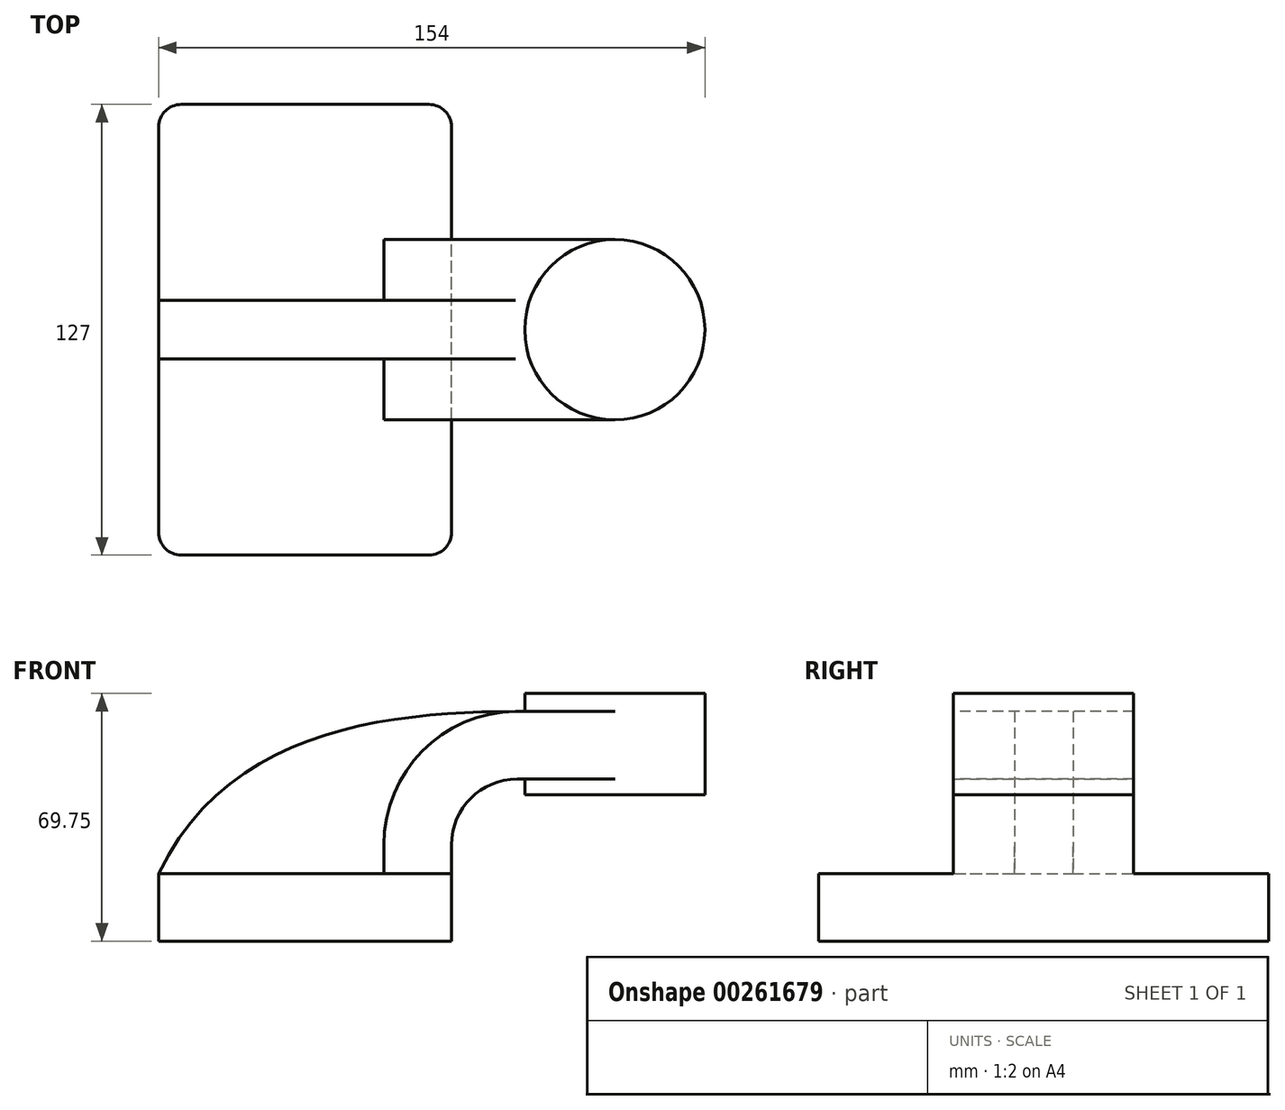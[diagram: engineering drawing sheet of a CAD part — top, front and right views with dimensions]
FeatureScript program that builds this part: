
annotation { "Feature Type Name" : "Feature", "Feature Type Description" : "" }
export const myFeature = defineFeature(function(context is Context, id is Id, definition is map)
    precondition{}
    {
        {
            var Q0;
            Q0=qCreatedBy(makeId("Front.planeOp"),FACE);
            var sketch = newSketch(context, id + "F0", { "sketchPlane" : qUnion([Q0])});
            skLineSegment(sketch, "E0.bottom", {"start": v(-41.28, -9.53) * mm, "end": v(41.28, -9.53) * mm});
            skLineSegment(sketch, "E0.top", {"start": v(-41.28, 9.53) * mm, "end": v(41.28, 9.53) * mm});
            skLineSegment(sketch, "E0.left", {"start": v(-41.28, -9.53) * mm, "end": v(-41.28, 9.53) * mm});
            skLineSegment(sketch, "E0.right", {"start": v(41.28, -9.53) * mm, "end": v(41.28, 9.53) * mm});
            skPoint(sketch, "E0.middle", {"position": v(0, 0) * mm});
            skLineSegment(sketch, "E1.bottom", {"start": v(112.72, 31.64) * mm, "end": v(61.92, 31.64) * mm});
            skLineSegment(sketch, "E1.top", {"start": v(112.72, 60.22) * mm, "end": v(61.92, 60.22) * mm});
            skLineSegment(sketch, "E1.left", {"start": v(112.72, 31.64) * mm, "end": v(112.72, 60.22) * mm});
            skLineSegment(sketch, "E1.right", {"start": v(61.92, 31.64) * mm, "end": v(61.92, 60.22) * mm});
            skPoint(sketch, "E1.middle", {"position": v(87.32, 45.93) * mm});
            skLineSegment(sketch, "E2", {"start": v(41.28, 9.53) * mm, "end": v(41.28, 17.63) * mm});
            skArc(sketch, "E3", {"start": v(41.28, 17.63) * mm, "mid": v(46.7, 30.71) * mm, "end": v(59.78, 36.13) * mm});
            skLineSegment(sketch, "E4", {"start": v(59.78, 36.13) * mm, "end": v(87.32, 36.13) * mm});
            skArc(sketch, "E5.1", {"start": v(22.23, 17.63) * mm, "mid": v(33.22, 44.18) * mm, "end": v(59.78, 55.18) * mm});
            skLineSegment(sketch, "E5.2", {"start": v(22.23, 9.53) * mm, "end": v(22.23, 17.63) * mm});
            skPoint(sketch, "E6.endSnap0", {"position": v(87.32, 31.64) * mm});
            skLineSegment(sketch, "E7", {"start": v(59.78, 55.18) * mm, "end": v(87.32, 55.18) * mm});
            skLineSegment(sketch, "E8", {"start": v(87.32, 60.22) * mm, "end": v(87.32, 31.64) * mm});
            skFitSpline(sketch, "E9", {"points": [v(59.78, 55.18) * mm, v(-41.28, 9.53) * mm], "startDerivative": vector(-106.5, -0.65) * mm, "endDerivative": vector(-59.81, -124.07) * mm});
            skSolve(sketch);
        }
        {
            var Q0;
            Q0=makeQuery(id+"F0.imprint","IMPRINT",FACE,{"disambiguationData":[TD([[makeQuery(id+"F0.imprint","IMPRINT",EDGE,{"derivedFrom":sQuery(id+"F0.wireOp",EDGE,"E0.bottom")}),1.0]])]});
            extrude(context, id + "F1", {"entities" : qUnion([Q0]), "endBound" : BoundingType.SYMMETRIC, "depth" : 127 * mm});
        }
        {
            var Q0;
            {var subQ6=sQuery(id+"F0.wireOp",EDGE,"E2");Q0=makeQuery(id+"F0.imprint","IMPRINT",FACE,{"disambiguationData":[TD([[makeQuery(id+"F0.imprint","IMPRINT",EDGE,{"derivedFrom":subQ6}),1.0]])]});}
            var Q1;
            {var subQ0=sQuery(id+"F0.wireOp",EDGE,"E4");var subQ1=sQuery(id+"F0.wireOp",EDGE,"E1.right");var subQ2=makeQuery(id+"F0.imprint","INTERSECT",VERTEX,{"derivedFrom":[subQ1,subQ0]});Q1=makeQuery(id+"F0.imprint","IMPRINT",FACE,{"disambiguationData":[TD([[makeQuery(id+"F0.imprint","IMPRINT",EDGE,{"disambiguationData":[TD([[subQ2,-1.0]])],"derivedFrom":subQ1}),-1.0]])]});}
            extrude(context, id + "F2", {"entities" : qUnion([Q0, Q1]), "operationType" : NewBodyOperationType.ADD, "endBound" : BoundingType.SYMMETRIC, "depth" : 50.8 * mm});
        }
        {
            var Q0;
            {var subQ3=sQuery(id+"F0.wireOp",EDGE,"E5.2");Q0=makeQuery(id+"F0.imprint","IMPRINT",FACE,{"disambiguationData":[TD([[makeQuery(id+"F0.imprint","IMPRINT",EDGE,{"derivedFrom":subQ3}),1.0]])]});}
            extrude(context, id + "F3", {"entities" : qUnion([Q0]), "operationType" : NewBodyOperationType.ADD, "endBound" : BoundingType.SYMMETRIC, "depth" : 16.5 * mm});
        }
        {
            var Q0;
            {var subQ0=sQuery(id+"F0.wireOp",EDGE,"E1.left");Q0=makeQuery(id+"F0.imprint","IMPRINT",FACE,{"disambiguationData":[TD([[makeQuery(id+"F0.imprint","IMPRINT",EDGE,{"derivedFrom":subQ0}),1.0]])]});}
            var Q1;
            Q1=sQuery(id+"F0.wireOp",EDGE,"E8");
            var Q2;
            Q2=sQuery(id+"F0.wireOp",EDGE,"E8");
            revolve(context, id + "F4", {"operationType" : NewBodyOperationType.ADD, "entities" : qUnion([Q0]), "surfaceEntities" : qUnion([Q1]), "axis" : qUnion([Q2]), "revolveType" : RevolveType.FULL});
        }
        {
            var Q0;
            Q0=makeQuery(id+"F1.opExtrude","CAP_EDGE",EDGE,{"disambiguationData":[OSD([sQuery(id+"F0.wireOp",EDGE,"E0.left")])],"isStart":false});
            var Q1;
            Q1=makeQuery(id+"F1.opExtrude","CAP_EDGE",EDGE,{"disambiguationData":[OSD([sQuery(id+"F0.wireOp",EDGE,"E0.right")])],"isStart":false});
            var Q2;
            Q2=makeQuery(id+"F1.opExtrude","CAP_EDGE",EDGE,{"disambiguationData":[OSD([sQuery(id+"F0.wireOp",EDGE,"E0.left")])],"isStart":true});
            var Q3;
            Q3=makeQuery(id+"F1.opExtrude","CAP_EDGE",EDGE,{"disambiguationData":[OSD([sQuery(id+"F0.wireOp",EDGE,"E0.right")])],"isStart":true});
            fillet(context, id + "F5", {"entities" : qUnion([Q0, Q1, Q2, Q3]), "radius" : 6.35 * mm, "tangentPropagation" : true, "allowEdgeOverflow" : false});
        }
    });
